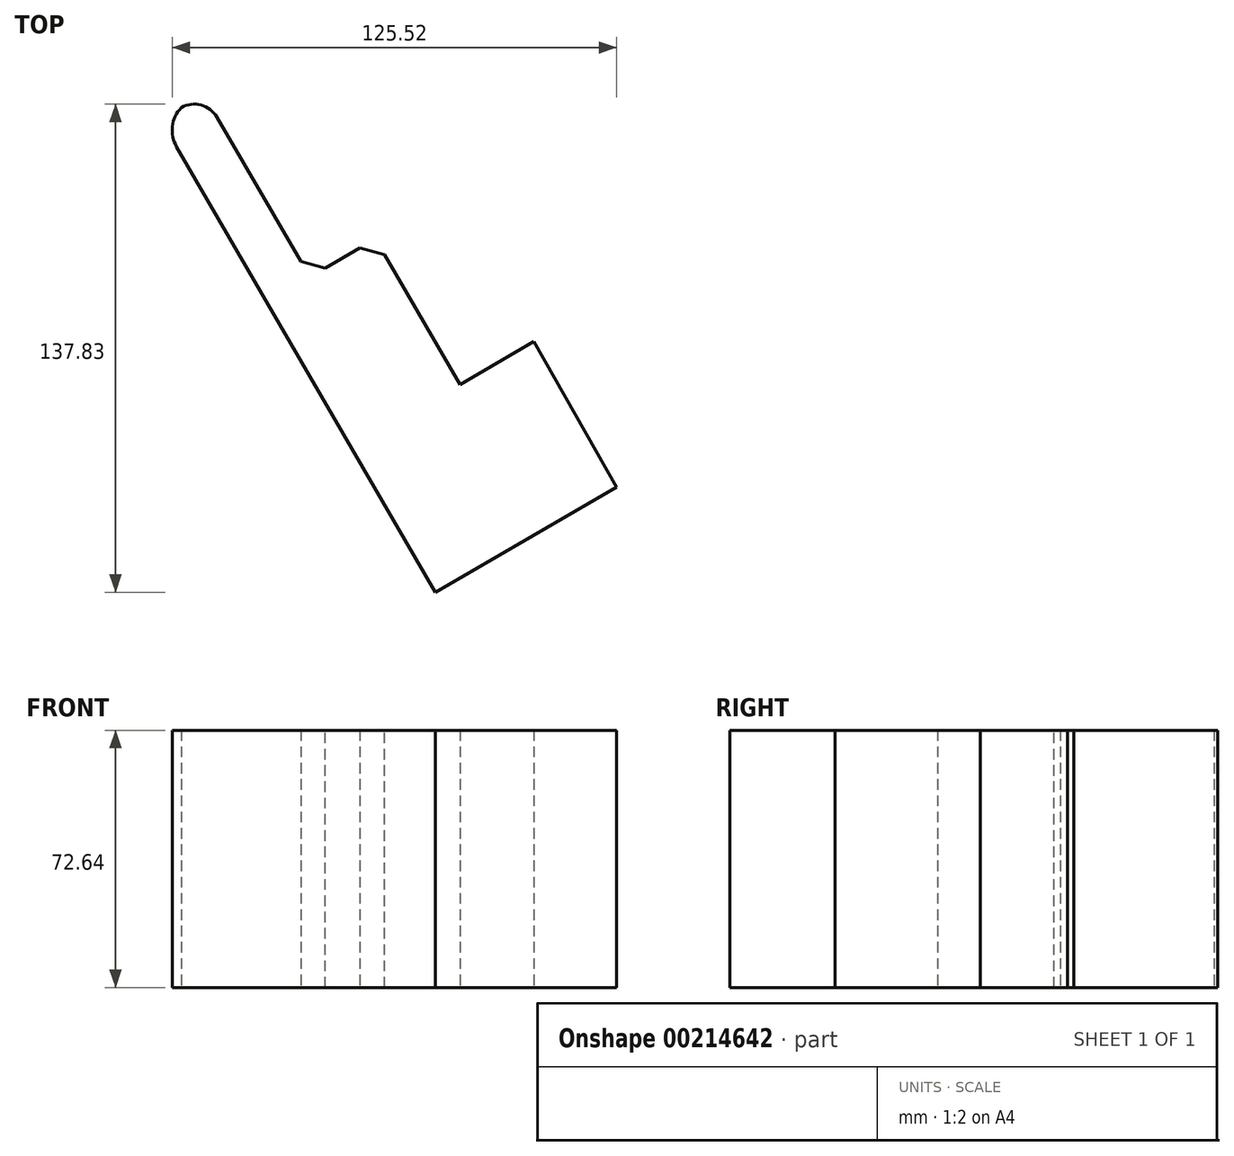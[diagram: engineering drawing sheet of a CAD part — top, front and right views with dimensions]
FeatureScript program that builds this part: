
annotation { "Feature Type Name" : "Feature", "Feature Type Description" : "" }
export const myFeature = defineFeature(function(context is Context, id is Id, definition is map)
    precondition{}
    {
        {
            var Q0;
            Q0=qCreatedBy(makeId("Top.planeOp"),FACE);
            var sketch = newSketch(context, id + "F0", { "sketchPlane" : qUnion([Q0])});
            skLineSegment(sketch, "E0", {"start": v(-36.74, 62.73) * mm, "end": v(40.86, -70.77) * mm});
            skLineSegment(sketch, "E1", {"start": v(-36.74, 62.73) * mm, "end": v(-24.64, 69.76) * mm});
            skLineSegment(sketch, "E2", {"start": v(-24.64, 69.76) * mm, "end": v(5.33, 18.2) * mm});
            skLineSegment(sketch, "E3", {"start": v(5.33, 18.2) * mm, "end": v(23.91, 29) * mm});
            skLineSegment(sketch, "E4", {"start": v(23.91, 29) * mm, "end": v(47.8, -12.1) * mm});
            skLineSegment(sketch, "E5", {"start": v(47.8, -12.1) * mm, "end": v(68.64, 0) * mm});
            skLineSegment(sketch, "E6", {"start": v(40.86, -70.77) * mm, "end": v(91.98, -41.06) * mm});
            skLineSegment(sketch, "E7", {"start": v(68.64, 0) * mm, "end": v(91.98, -41.06) * mm});
            skSolve(sketch);
        }
        {
            var Q0;
            Q0 = qSketchRegion(id + "F0", true);
            extrude(context, id + "F1", {"entities" : qUnion([Q0]), "depth" : 72.64 * mm});
        }
        {
            var Q0;
            Q0=makeQuery(id+"F1.opExtrude","SWEPT_EDGE",EDGE,{"disambiguationData":[OSD([sQuery(id+"F0.wireOp",EDGE,"E1"),sQuery(id+"F0.wireOp",EDGE,"E2")])]});
            fillet(context, id + "F2", {"entities" : qUnion([Q0]), "radius" : 7.36 * mm, "tangentPropagation" : true, "allowEdgeOverflow" : false});
        }
        {
            var Q0;
            Q0=makeQuery(id+"F1.opExtrude","SWEPT_EDGE",EDGE,{"disambiguationData":[OSD([sQuery(id+"F0.wireOp",EDGE,"E2"),sQuery(id+"F0.wireOp",EDGE,"E3")])]});
            chamfer(context, id + "F3", {"entities" : qUnion([Q0]), "width" : 5.08 * mm, "tangentPropagation" : true});
        }
        {
            var Q0;
            Q0=makeQuery(id+"F1.opExtrude","SWEPT_EDGE",EDGE,{"disambiguationData":[OSD([sQuery(id+"F0.wireOp",EDGE,"E3"),sQuery(id+"F0.wireOp",EDGE,"E4")])]});
            chamfer(context, id + "F4", {"entities" : qUnion([Q0]), "width" : 5.08 * mm, "tangentPropagation" : true});
        }
        {
            var Q0;
            Q0=makeQuery(id+"F1.opExtrude","SWEPT_EDGE",EDGE,{"disambiguationData":[OSD([sQuery(id+"F0.wireOp",EDGE,"E0"),sQuery(id+"F0.wireOp",EDGE,"E1")])]});
            fillet(context, id + "F5", {"entities" : qUnion([Q0]), "radius" : 9.2 * mm, "tangentPropagation" : true, "allowEdgeOverflow" : false});
        }
    });
